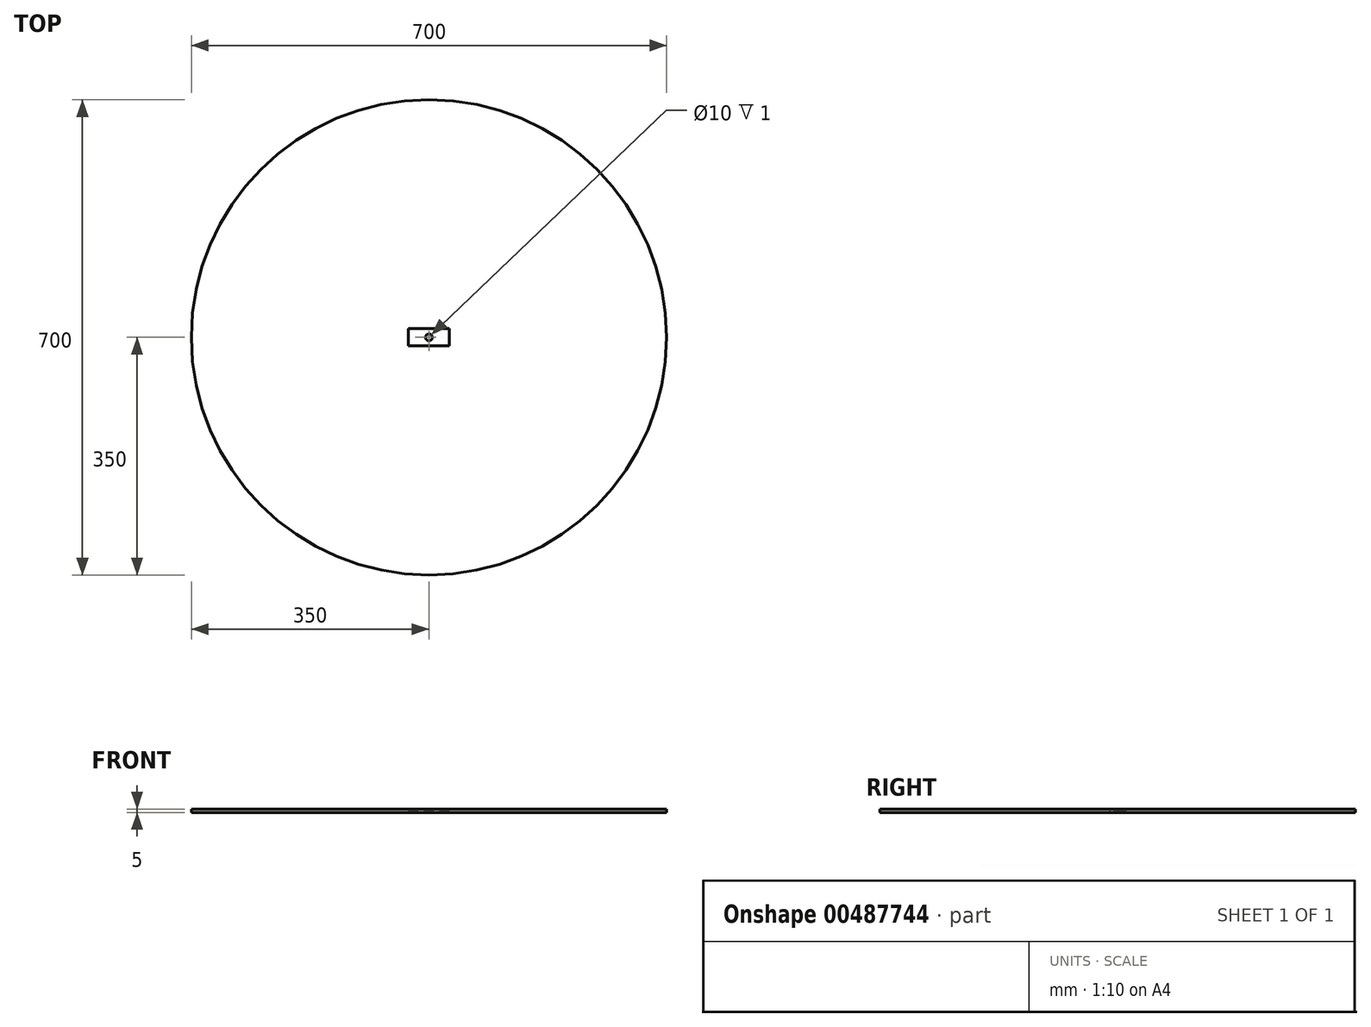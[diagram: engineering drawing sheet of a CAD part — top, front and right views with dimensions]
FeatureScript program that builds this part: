
annotation { "Feature Type Name" : "Feature", "Feature Type Description" : "" }
export const myFeature = defineFeature(function(context is Context, id is Id, definition is map)
    precondition{}
    {
        {
            var Q0;
            Q0=qCreatedBy(makeId("Top.planeOp"),FACE);
            var sketch = newSketch(context, id + "F0", { "sketchPlane" : qUnion([Q0])});
            skCircle(sketch, "E0", {"center": v(0, 0) * mm, "radius": 350 * mm});
            skLineSegment(sketch, "E1.bottom", {"start": v(30.25, 12.75) * mm, "end": v(-30.25, 12.75) * mm});
            skLineSegment(sketch, "E1.top", {"start": v(30.25, -12.75) * mm, "end": v(-30.25, -12.75) * mm});
            skLineSegment(sketch, "E1.left", {"start": v(30.25, 12.75) * mm, "end": v(30.25, -12.75) * mm});
            skLineSegment(sketch, "E1.right", {"start": v(-30.25, 12.75) * mm, "end": v(-30.25, -12.75) * mm});
            skSolve(sketch);
        }
        {
            var Q0;
            Q0=makeQuery(id+"F0.imprint","IMPRINT",FACE,{"disambiguationData":[TD([[makeQuery(id+"F0.imprint","IMPRINT",EDGE,{"derivedFrom":sQuery(id+"F0.wireOp",EDGE,"E0")}),1.0]])]});
            var Q1;
            Q1=makeQuery(id+"F0.imprint","IMPRINT",FACE,{"disambiguationData":[TD([[makeQuery(id+"F0.imprint","IMPRINT",EDGE,{"derivedFrom":sQuery(id+"F0.wireOp",EDGE,"E1.bottom")}),1.0]])]});
            extrude(context, id + "F1", {"entities" : qUnion([Q0, Q1]), "oppositeDirection" : true, "depth" : 5 * mm});
        }
        {
            var Q0;
            Q0=makeQuery(id+"F0.imprint","IMPRINT",FACE,{"disambiguationData":[TD([[makeQuery(id+"F0.imprint","IMPRINT",EDGE,{"derivedFrom":sQuery(id+"F0.wireOp",EDGE,"E1.bottom")}),1.0]])]});
            extrude(context, id + "F2", {"entities" : qUnion([Q0]), "operationType" : NewBodyOperationType.REMOVE, "oppositeDirection" : true, "depth" : 2 * mm});
        }
        {
            var Q0;
            Q0=makeQuery(id+"F2.boolean.opBoolean","COPY",FACE,{"derivedFrom":makeQuery(id+"F2.opExtrude","CAP_FACE",FACE,{"disambiguationData":[OSD([sQuery(id+"F0.wireOp",EDGE,"E1.bottom"),sQuery(id+"F0.wireOp",EDGE,"E1.top"),sQuery(id+"F0.wireOp",EDGE,"E1.left"),sQuery(id+"F0.wireOp",EDGE,"E1.right")])],"isStart":false})});
            var sketch = newSketch(context, id + "F3", { "sketchPlane" : qUnion([Q0])});
            skCircle(sketch, "E2", {"center": v(0, 0) * mm, "radius": 5 * mm});
            skSolve(sketch);
        }
        {
            var Q0;
            Q0 = qSketchRegion(id + "F3", true);
            extrude(context, id + "F4", {"entities" : qUnion([Q0]), "operationType" : NewBodyOperationType.REMOVE, "oppositeDirection" : true, "depth" : 1 * mm});
        }
    });
